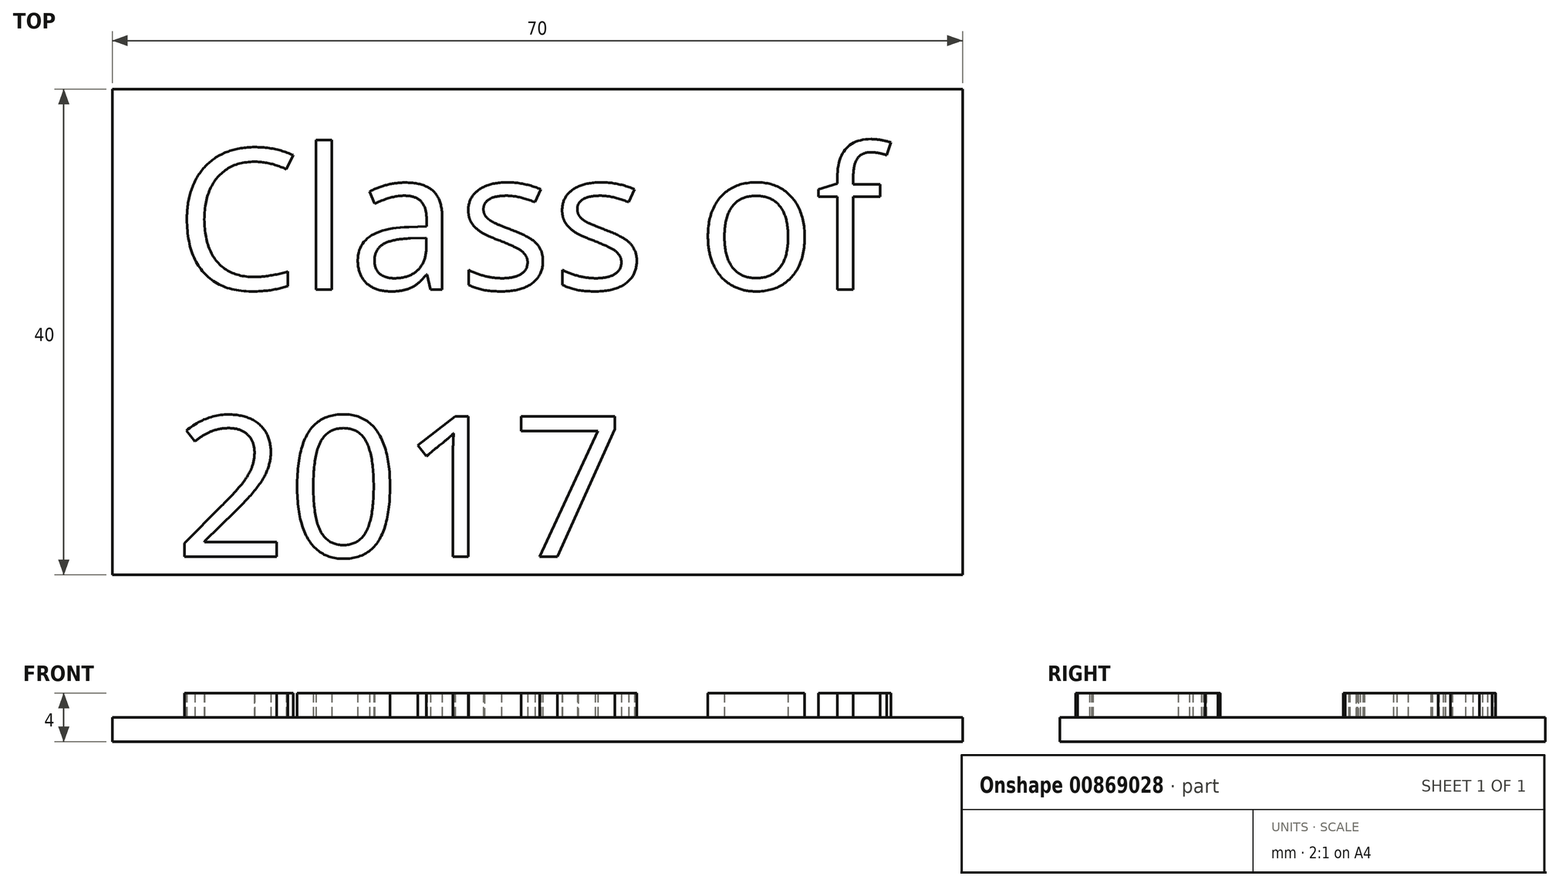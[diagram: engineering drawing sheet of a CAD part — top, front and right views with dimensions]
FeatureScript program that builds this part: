
annotation { "Feature Type Name" : "Feature", "Feature Type Description" : "" }
export const myFeature = defineFeature(function(context is Context, id is Id, definition is map)
    precondition{}
    {
        {
            var Q0;
            Q0=qCreatedBy(makeId("Top.planeOp"),FACE);
            var sketch = newSketch(context, id + "F0", { "sketchPlane" : qUnion([Q0])});
            skLineSegment(sketch, "E0.bottom", {"start": v(0, 0) * mm, "end": v(70, 0) * mm});
            skLineSegment(sketch, "E0.top", {"start": v(0, -40) * mm, "end": v(70, -40) * mm});
            skLineSegment(sketch, "E0.left", {"start": v(0, 0) * mm, "end": v(0, -40) * mm});
            skLineSegment(sketch, "E0.right", {"start": v(70, 0) * mm, "end": v(70, -40) * mm});
            skSolve(sketch);
        }
        {
            var Q0;
            Q0=makeQuery(id+"F0.imprint","IMPRINT",FACE,{"disambiguationData":[TD([[makeQuery(id+"F0.imprint","IMPRINT",EDGE,{"derivedFrom":sQuery(id+"F0.wireOp",EDGE,"E0.bottom")}),-1.0]])]});
            extrude(context, id + "F1", {"entities" : qUnion([Q0]), "depth" : 2 * mm, "offsetDistance" : 25 * mm});
        }
        {
            var Q0;
            Q0=qCreatedBy(makeId("Top.planeOp"),FACE);
            var sketch = newSketch(context, id + "F2", { "sketchPlane" : qUnion([Q0])});
            skText(sketch, "E1", { "text": "Class of \n2017\n", "fontName": "OpenSans-Regular.ttf"});
            const initialGuessF2  = {"E1": [0.00515, -0.0165, 1, 0, 0.01166]};
            skSetInitialGuess(sketch, initialGuessF2);
            skSolve(sketch);
        }
        {
            var Q0;
            Q0 = qSketchRegion(id + "F2", true);
            extrude(context, id + "F3", {"entities" : qUnion([Q0]), "operationType" : NewBodyOperationType.ADD, "depth" : 4 * mm, "offsetDistance" : 25 * mm});
        }
    });
